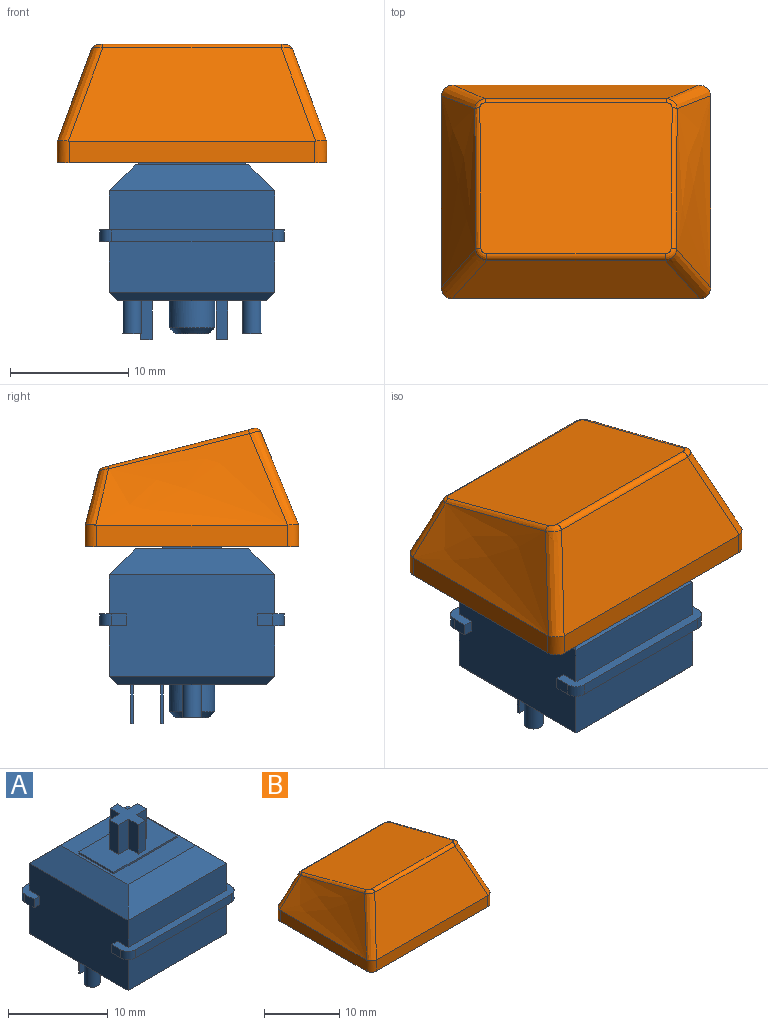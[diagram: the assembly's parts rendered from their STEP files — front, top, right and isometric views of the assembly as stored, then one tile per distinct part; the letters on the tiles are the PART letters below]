
ASSEMBLY  parts=2 mates=1
PART A: 69 faces, bbox 15.6x15.6x18.6 mm
  f0: plane 15.6x2.3mm, normal (0,0,-1), area 14.4mm2, adj f2,f3,f28,f30,f35,f60,f62,f63
  f1: plane 15.6x2.3mm, normal (0,0,-1), area 14.4mm2, adj f28,f30,f33,f34,f36,f59,f61,f64
  f2: plane 1.3x1mm, normal (1,0,0), area 1.3mm2, adj f0,f32,f62,f66
  f3: plane 1.3x1mm, normal (-1,0,0), area 1.3mm2, adj f0,f32,f63,f68
  f4: plane 15.6x2.3mm, normal (0,0,1), area 14.4mm2, adj f28,f30,f31,f33,f34,f36,f61,f64
  f5: plane 14x2.2mm, normal (-0.71,0,0.71), area 36.7mm2, adj f6,f7,f26,f30
  f6: plane 14x2.2mm, normal (0,-0.71,0.71), area 36.7mm2, adj f5,f7,f27,f31
  f7: plane 9.6x9.6mm, normal (0,0,1), area 47.2mm2, adj f5,f6,f8,f9,f10,f11,f26,f27
  f8: plane 5x0.2mm, normal (1,0,0), area 1mm2, adj f7,f9,f11,f12
  f9: plane 9x0.2mm, normal (0,1,0), area 1.8mm2, adj f7,f8,f10,f12
  f10: plane 5x0.2mm, normal (-1,0,0), area 1mm2, adj f7,f9,f11,f12
  f11: plane 9x0.2mm, normal (0,-1,0), area 1.8mm2, adj f7,f8,f10,f12
  f12: plane 9x5mm, normal (0,0,1), area 36.9mm2, adj f8,f9,f10,f11,f13,f14,f15,f16
  f13: plane 3.6x1.35mm, normal (1,0,0), area 4.9mm2, adj f12,f14,f24,f25
  f14: plane 3.6x1.08mm, normal (0,1,0), area 3.9mm2, adj f12,f13,f15,f25
  f15: plane 3.6x1.35mm, normal (-1,0,0), area 4.9mm2, adj f12,f14,f16,f25
  f16: plane 3.6x1.46mm, normal (0,1,0), area 5.3mm2, adj f12,f15,f17,f25
  f17: plane 3.6x1.3mm, normal (-1,0,0), area 4.7mm2, adj f12,f16,f18,f25
  f18: plane 3.6x1.46mm, normal (0,-1,0), area 5.3mm2, adj f12,f17,f19,f25
  f19: plane 3.6x1.35mm, normal (-1,0,0), area 4.9mm2, adj f12,f18,f20,f25
  f20: plane 3.6x1.08mm, normal (0,-1,0), area 3.9mm2, adj f12,f19,f21,f25
  f21: plane 3.6x1.35mm, normal (1,0,0), area 4.9mm2, adj f12,f20,f22,f25
  f22: plane 3.6x1.46mm, normal (0,-1,0), area 5.3mm2, adj f12,f21,f23,f25
  f23: plane 3.6x1.3mm, normal (1,0,0), area 4.7mm2, adj f12,f22,f24,f25
  f24: plane 3.6x1.46mm, normal (0,1,0), area 5.3mm2, adj f12,f13,f23,f25
  f25: plane 4x4mm, normal (0,0,1), area 8.1mm2, adj f13,f14,f15,f16,f17,f18,f19,f20
  f26: plane 14x2.2mm, normal (0,0.71,0.71), area 36.7mm2, adj f5,f7,f27,f29
  f27: plane 14x2.2mm, normal (0.71,0,0.71), area 36.7mm2, adj f6,f7,f26,f28
  f28: plane 14x8.6mm, normal (1,0,0), area 117.4mm2, adj f0,f1,f4,f27,f29,f31,f32,f55
  f29: plane 14x3.3mm, normal (0,1,0), area 46.2mm2, adj f26,f28,f30,f32
  f30: plane 14x8.6mm, normal (-1,0,0), area 117.4mm2, adj f0,f1,f4,f5,f29,f31,f32,f57
  f31: plane 14x3.3mm, normal (0,-1,0), area 46.2mm2, adj f4,f6,f28,f30
  f32: plane 15.6x2.3mm, normal (0,0,1), area 14.4mm2, adj f2,f3,f28,f29,f30,f35,f62,f63
  f33: plane 13.6x1mm, normal (0,-1,0), area 13.6mm2, adj f1,f4,f61,f64
  f34: plane 1.3x1mm, normal (1,0,0), area 1.3mm2, adj f1,f4,f61,f65
  f35: plane 13.6x1mm, normal (0,1,0), area 13.6mm2, adj f0,f32,f62,f63
  f36: plane 1.3x1mm, normal (-1,0,0), area 1.3mm2, adj f1,f4,f64,f67
  f37: plane 2.85x2.85mm, normal (0,0,-1), area 6.4mm2, adj f38
  f38: cone r=1.43mm half-angle=45deg, axis (0,0,1), area 7.4mm2, adj f37,f43
  f39: plane 1x0.2mm, normal (0,0,-1), area 0.2mm2, adj f44,f45,f46,f47
  f40: plane 1x0.2mm, normal (0,0,-1), area 0.2mm2, adj f48,f49,f50,f51
  f41: plane 1.6x1.6mm, normal (0,0,-1), area 2mm2, adj f52
  f42: plane 1.6x1.6mm, normal (0,0,-1), area 2mm2, adj f53
  f43: cylinder r=1.93mm len=3.85mm, axis (0,0,1), area 27.8mm2, adj f38,f54
  f44: plane 3.3x0.2mm, normal (-1,0,0), area 0.7mm2, adj f39,f45,f47,f54
  f45: plane 3.3x1mm, normal (0,1,0), area 3.3mm2, adj f39,f44,f46,f54
  f46: plane 3.3x0.2mm, normal (1,0,0), area 0.7mm2, adj f39,f45,f47,f54
  f47: plane 3.3x1mm, normal (0,-1,0), area 3.3mm2, adj f39,f44,f46,f54
  f48: plane 3.3x0.2mm, normal (-1,0,0), area 0.7mm2, adj f40,f49,f51,f54
  f49: plane 3.3x1mm, normal (0,1,0), area 3.3mm2, adj f40,f48,f50,f54
  f50: plane 3.3x0.2mm, normal (1,0,0), area 0.7mm2, adj f40,f49,f51,f54
  f51: plane 3.3x1mm, normal (0,-1,0), area 3.3mm2, adj f40,f48,f50,f54
  f52: cylinder r=0.8mm len=2.8mm, axis (0,0,1), area 14.1mm2, adj f41,f54
  f53: cylinder r=0.8mm len=2.8mm, axis (0,0,1), area 14.1mm2, adj f42,f54
  f54: plane 12.6x12.6mm, normal (0,0,-1), area 142.7mm2, adj f43,f44,f45,f46,f47,f48,f49,f50
  f55: plane 14x0.7mm, normal (0.71,0,-0.71), area 13.2mm2, adj f28,f54,f56,f58
  f56: plane 14x0.7mm, normal (0,0.71,-0.71), area 13.2mm2, adj f54,f55,f57,f60
  f57: plane 14x0.7mm, normal (-0.71,0,-0.71), area 13.2mm2, adj f30,f54,f56,f58
  f58: plane 14x0.7mm, normal (0,-0.71,-0.71), area 13.2mm2, adj f54,f55,f57,f59
  f59: plane 14x4.3mm, normal (0,-1,0), area 60.2mm2, adj f1,f28,f30,f58
  f60: plane 14x4.3mm, normal (0,1,0), area 60.2mm2, adj f0,f28,f30,f56
  f61: cylinder r=1mm len=1mm, axis (0,0,-1), area 1.6mm2, adj f1,f4,f33,f34
  f62: cylinder r=1mm len=1mm, axis (0,0,1), area 1.6mm2, adj f0,f2,f32,f35
  f63: cylinder r=1mm len=1mm, axis (0,0,-1), area 1.6mm2, adj f0,f3,f32,f35
  f64: cylinder r=1mm len=1mm, axis (0,0,1), area 1.6mm2, adj f1,f4,f33,f36
  f65: plane 1x0.8mm, normal (0,1,0), area 0.8mm2, adj f1,f4,f28,f34
  f66: plane 1x0.8mm, normal (0,-1,0), area 0.8mm2, adj f0,f2,f28,f32
  f67: plane 1x0.8mm, normal (0,1,0), area 0.8mm2, adj f1,f4,f30,f36
  f68: plane 1x0.8mm, normal (0,-1,0), area 0.8mm2, adj f0,f3,f30,f32
PART B: 50 faces, bbox 27.1x22.7x14.6 mm
  f0: plane 18.58x14.91mm, normal (0,-0.25,-0.97), area 169mm2, adj f31,f32,f33,f34,f47
  f1: plane 22.81x18.1mm, normal (0,0,-1), area 77mm2, adj f2,f3,f4,f5,f11,f13,f15,f17
  f2: plane 20.81x1.8mm, normal (0,-1,0), area 37.5mm2, adj f1,f9,f11,f13
  f3: plane 16.1x1.8mm, normal (1,0,0), area 29mm2, adj f1,f10,f11,f17
  f4: plane 20.81x1.8mm, normal (0,1,0), area 37.5mm2, adj f1,f7,f15,f16,f17,f18
  f5: plane 16.1x1.8mm, normal (-1,0,0), area 29mm2, adj f1,f8,f13,f15
  f6: plane 16.27x12.77mm, normal (0,0.25,0.97), area 213.1mm2, adj f19,f20,f21,f22,f23,f24,f25,f26
  f7: plane 20.78x4.53mm, normal (0,0.97,0.25), area 84.4mm2, adj f4,f16,f18,f21
  f8: bspline ~18.1x8.31mm, area 98.6mm2, adj f5,f13,f14,f15,f16,f20
  f9: plane 20.96x7.9mm, normal (0,-0.93,0.38), area 153.9mm2, adj f2,f11,f12,f13,f14,f24
  f10: bspline ~18.1x8.31mm, area 98.6mm2, adj f3,f11,f12,f17,f18,f25
  f11: cylinder r=1mm len=1.87mm, axis (0,0,1), area 2.9mm2, adj f1,f2,f3,f9,f10,f12
  f12: bspline ~11.3x5.51mm, area 13.2mm2, adj f9,f10,f11,f26
  f13: cylinder r=1mm len=1.87mm, axis (0,0,-1), area 2.9mm2, adj f1,f2,f5,f8,f9,f14
  f14: bspline ~11.44x5.57mm, area 13.2mm2, adj f8,f9,f13,f22
  f15: cylinder r=1mm len=1.81mm, axis (0,0,1), area 2.8mm2, adj f1,f4,f5,f8,f16
  f16: bspline ~7.23x4.95mm, area 7.7mm2, adj f4,f7,f8,f15,f19
  f17: cylinder r=1mm len=1.81mm, axis (0,0,-1), area 2.8mm2, adj f1,f3,f4,f10,f18
  f18: bspline ~7.14x4.9mm, area 7.7mm2, adj f4,f7,f10,f17,f23
  f19: bspline ~1.16x0.9mm, area 0.5mm2, adj f6,f16,f20,f21
  f20: bspline ~18.2x4.87mm, area 7mm2, adj f6,f8,f19,f22
  f21: cylinder r=0.5mm len=15.39mm, axis (-1,0,0), area 8.2mm2, adj f6,f7,f19,f23
  f22: bspline ~1.24x1.04mm, area 0.8mm2, adj f6,f14,f20,f24
  f23: bspline ~1.09x0.94mm, area 0.5mm2, adj f6,f18,f21,f25
  f24: cylinder r=0.5mm len=15.09mm, axis (-1,0,0), area 10.8mm2, adj f6,f9,f22,f26
  f25: bspline ~15.84x4.3mm, area 7mm2, adj f6,f10,f23,f26
  f26: bspline ~1.22x1.1mm, area 0.8mm2, adj f6,f12,f24,f25
  f27: plane 20.81x1.61mm, normal (0,1,0), area 33.4mm2, adj f1,f28,f30,f33
  f28: plane 16.18x1.7mm, normal (-1,0,0), area 25.4mm2, adj f1,f27,f29,f34
  f29: plane 20.81x1.67mm, normal (0,-1,0), area 34.8mm2, adj f1,f28,f30,f31,f32,f34
  f30: plane 16.18x1.7mm, normal (1,0,0), area 25.4mm2, adj f1,f27,f29,f32
  f31: plane 20.64x4.13mm, normal (0,-0.97,-0.25), area 77.2mm2, adj f0,f29,f32,f34
  f32: offset ~20.1x10.31mm, area 90.9mm2, adj f0,f29,f30,f31,f33
  f33: plane 20.86x7.36mm, normal (0,0.93,-0.38), area 143.1mm2, adj f0,f27,f32,f34
  f34: offset ~20.1x10.31mm, area 90.8mm2, adj f0,f28,f29,f31,f33
  f35: plane 7.09x1mm, normal (0,-1,0), area 7.1mm2, adj f36,f46,f48,f49
  f36: plane 7.44x1.35mm, normal (-1,0,0), area 9.8mm2, adj f35,f37,f48,f49
  f37: plane 7.44x1.5mm, normal (0,-1,0), area 11.2mm2, adj f36,f38,f48,f49
  f38: plane 7.77x1.3mm, normal (-1,0,0), area 9.9mm2, adj f37,f39,f48,f49
  f39: plane 7.77x1.5mm, normal (0,1,0), area 11.7mm2, adj f38,f40,f48,f49
  f40: plane 8.12x1.35mm, normal (-1,0,0), area 10.7mm2, adj f39,f41,f48,f49
  f41: plane 8.12x1mm, normal (0,1,0), area 8.1mm2, adj f40,f42,f48,f49
  f42: plane 8.12x1.35mm, normal (1,0,0), area 10.7mm2, adj f41,f43,f48,f49
  f43: plane 7.77x1.5mm, normal (0,1,0), area 11.7mm2, adj f42,f44,f48,f49
  f44: plane 7.77x1.3mm, normal (1,0,0), area 9.9mm2, adj f43,f45,f48,f49
  f45: plane 7.44x1.5mm, normal (0,-1,0), area 11.2mm2, adj f44,f46,f48,f49
  f46: plane 7.44x1.35mm, normal (1,0,0), area 9.8mm2, adj f35,f45,f48,f49
  f47: cylinder r=2.75mm len=6.89mm, axis (0,0,-1), area 119.1mm2, adj f0,f48
  f48: plane 5.5x5.5mm, normal (0,0,-1), area 15.9mm2, adj f35,f36,f37,f38,f39,f40,f41,f42
  f49: plane 4x4mm, normal (0,-0.25,-0.97), area 8.2mm2, adj f35,f36,f37,f38,f39,f40,f41,f42
PLACE A at identity fixed
PLACE B t=(0,0,11.7)mm
MATE fastened B.f47 <-> A.f38  axis (0,0,-1) through (0,0,11.7)mm
